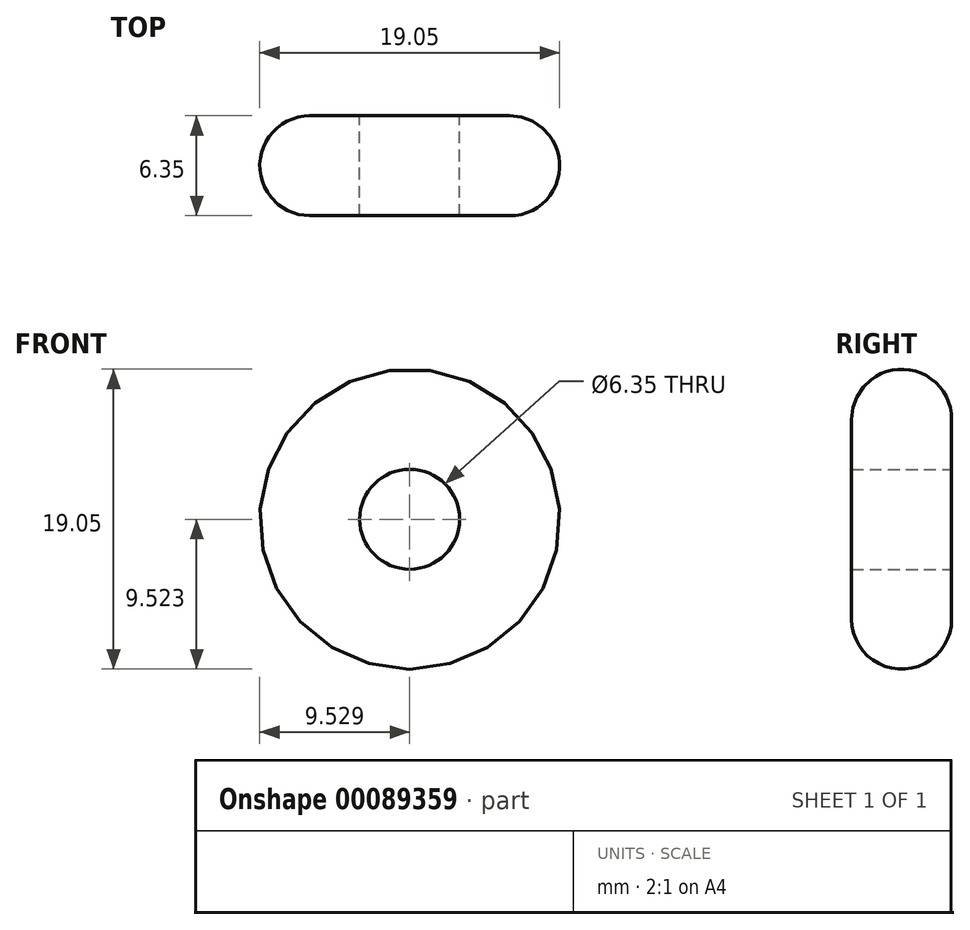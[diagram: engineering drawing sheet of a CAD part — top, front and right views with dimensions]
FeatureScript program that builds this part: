
annotation { "Feature Type Name" : "Feature", "Feature Type Description" : "" }
export const myFeature = defineFeature(function(context is Context, id is Id, definition is map)
    precondition{}
    {
        {
            var Q0;
            Q0=qCreatedBy(makeId("Front.planeOp"),FACE);
            var sketch = newSketch(context, id + "F0", { "sketchPlane" : qUnion([Q0])});
            skCircle(sketch, "E0", {"center": v(-29.44, 24.13) * mm, "radius": 9.53 * mm});
            skCircle(sketch, "E1", {"center": v(-29.44, 24.13) * mm, "radius": 3.18 * mm});
            skSolve(sketch);
        }
        {
            var Q0;
            Q0 = qSketchRegion(id + "F0", true);
            extrude(context, id + "F1", {"entities" : qUnion([Q0]), "depth" : 6.35 * mm});
        }
        {
            var Q0;
            Q0=makeQuery(id+"F1.opExtrude","SWEPT_FACE",FACE,{"disambiguationData":[OSD([sQuery(id+"F0.wireOp",EDGE,"E0")])]});
            fillet(context, id + "F2", {"entities" : qUnion([Q0]), "radius" : 3.17 * mm, "tangentPropagation" : true, "allowEdgeOverflow" : false});
        }
    });
